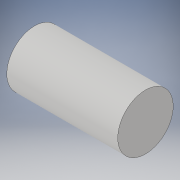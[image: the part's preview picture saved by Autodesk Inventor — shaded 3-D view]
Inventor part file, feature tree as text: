
AUTODESK INVENTOR PART (.ipt)
format: ipt  version: 2017 (Build 210142000, 142)  size: 87,552 bytes
history: native  units: in
note: dims shown in document units (in); Inventor stores cm internally (conversion verified against a paired STEP export)
features: extrude x1, sketch x1
ambient origin geometry x8: Origin, YZ Plane, XZ Plane, XY Plane, X Axis, Y Axis, Z Axis, Center Point
bodies: Solid1 (feature_tree)
feature tree (2):
  extrude  "Extrusion1"  Depth=10.0in TaperAngle=0.0deg
  sketch  "Sketch1"  dims[d0=5.0in d1=10.0in d2=0.0in]
